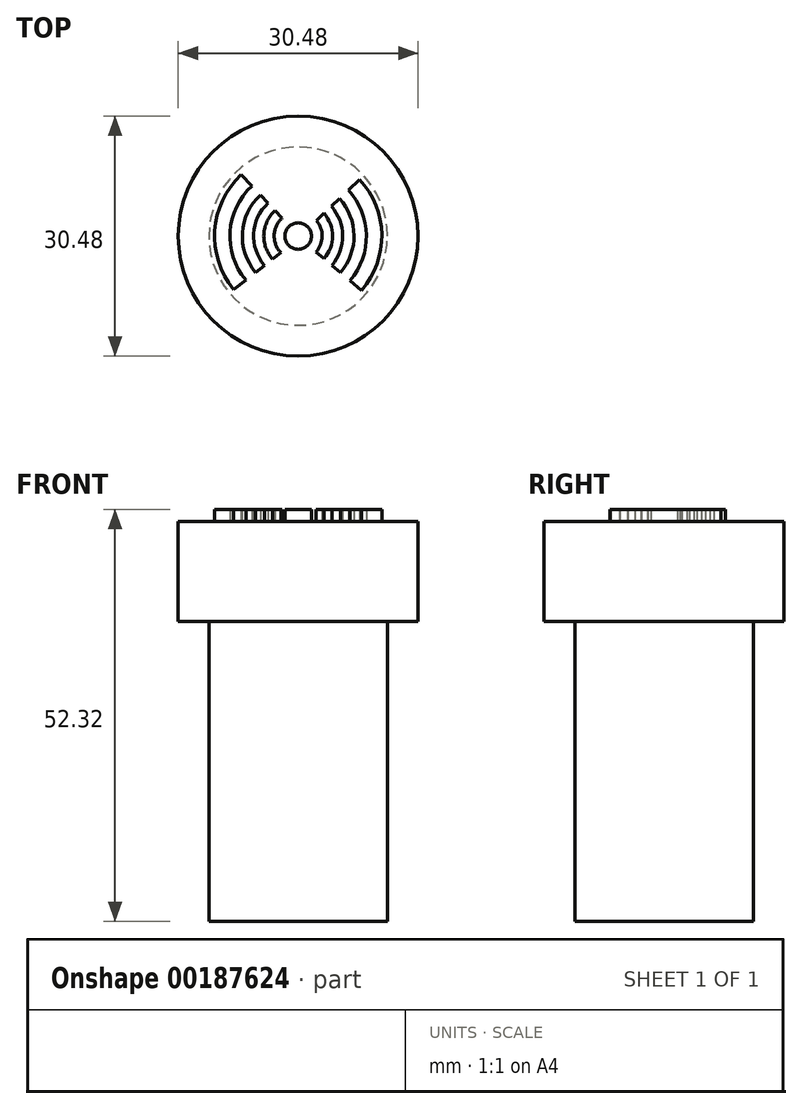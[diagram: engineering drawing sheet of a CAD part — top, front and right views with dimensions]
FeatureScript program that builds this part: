
annotation { "Feature Type Name" : "Feature", "Feature Type Description" : "" }
export const myFeature = defineFeature(function(context is Context, id is Id, definition is map)
    precondition{}
    {
        {
            var Q0;
            Q0=qCreatedBy(makeId("Top.planeOp"),FACE);
            var sketch = newSketch(context, id + "F0", { "sketchPlane" : qUnion([Q0])});
            skCircle(sketch, "E0", {"center": v(0, 0) * mm, "radius": 15.24 * mm});
            skCircle(sketch, "E1", {"center": v(0, 0) * mm, "radius": 11.33 * mm});
            skSolve(sketch);
        }
        {
            var Q0;
            Q0=makeQuery(id+"F0.imprint","IMPRINT",FACE,{"disambiguationData":[TD([[makeQuery(id+"F0.imprint","IMPRINT",EDGE,{"derivedFrom":sQuery(id+"F0.wireOp",EDGE,"E1")}),1.0]])]});
            extrude(context, id + "F1", {"entities" : qUnion([Q0]), "oppositeDirection" : true, "depth" : 50.8 * mm});
        }
        {
            var Q0;
            Q0 = qSketchRegion(id + "F0", true);
            extrude(context, id + "F2", {"entities" : qUnion([Q0]), "operationType" : NewBodyOperationType.ADD, "oppositeDirection" : true, "depth" : 12.7 * mm});
        }
        {
            var Q0;
            Q0=qCreatedBy(makeId("Top.planeOp"),FACE);
            var sketch = newSketch(context, id + "F3", { "sketchPlane" : qUnion([Q0])});
            skCircle(sketch, "E2", {"center": v(0, 0) * mm, "radius": 1.69 * mm});
            skArc(sketch, "E3", {"start": v(-2.02, 2.28) * mm, "mid": v(-3.04, 0.12) * mm, "end": v(-2.2, -2.12) * mm});
            skArc(sketch, "E4", {"start": v(-2.93, 3.24) * mm, "mid": v(-4.36, 0.22) * mm, "end": v(-3.24, -2.93) * mm});
            skArc(sketch, "E5", {"start": v(-3.82, 4.18) * mm, "mid": v(-5.65, 0.32) * mm, "end": v(-4.27, -3.72) * mm});
            skArc(sketch, "E6", {"start": v(-4.8, 5.22) * mm, "mid": v(-7.08, 0.43) * mm, "end": v(-5.4, -4.6) * mm});
            skArc(sketch, "E7", {"start": v(-5.89, 6.37) * mm, "mid": v(-8.66, 0.55) * mm, "end": v(-6.65, -5.57) * mm});
            skArc(sketch, "E8", {"start": v(-7.23, 7.78) * mm, "mid": v(-10.6, 0.7) * mm, "end": v(-8.2, -6.77) * mm});
            skLineSegment(sketch, "E9", {"start": v(-2.02, 2.28) * mm, "end": v(-2.93, 3.24) * mm});
            skLineSegment(sketch, "E10", {"start": v(2.3, 2) * mm, "end": v(3.26, 2.9) * mm});
            skLineSegment(sketch, "E11", {"start": v(-2.2, -2.12) * mm, "end": v(-3.24, -2.93) * mm});
            skLineSegment(sketch, "E12", {"start": v(2.27, -2.04) * mm, "end": v(3.28, -2.88) * mm});
            skArc(sketch, "E13.trimOffspring", {"start": v(3.28, -2.88) * mm, "mid": v(4.37, 0.01) * mm, "end": v(3.26, 2.9) * mm});
            skArc(sketch, "E14.trimOffspring", {"start": v(2.27, -2.04) * mm, "mid": v(3.05, -0.03) * mm, "end": v(2.3, 2) * mm});
            skArc(sketch, "E15.trimOffspring", {"start": v(4.28, -3.71) * mm, "mid": v(5.66, 0.05) * mm, "end": v(4.2, 3.79) * mm});
            skArc(sketch, "E16.trimOffspring", {"start": v(5.38, -4.63) * mm, "mid": v(7.1, 0.1) * mm, "end": v(5.25, 4.77) * mm});
            skArc(sketch, "E17.trimOffspring", {"start": v(6.59, -5.64) * mm, "mid": v(8.67, 0.14) * mm, "end": v(6.4, 5.85) * mm});
            skArc(sketch, "E18.trimOffspring", {"start": v(8.08, -6.9) * mm, "mid": v(10.62, 0.2) * mm, "end": v(7.82, 7.2) * mm});
            skLineSegment(sketch, "E19.trimOffspring", {"start": v(-3.82, 4.18) * mm, "end": v(-4.8, 5.22) * mm});
            skLineSegment(sketch, "E20.trimOffspring", {"start": v(-4.27, -3.72) * mm, "end": v(-5.4, -4.6) * mm});
            skLineSegment(sketch, "E21.trimOffspring", {"start": v(-6.65, -5.57) * mm, "end": v(-8.2, -6.77) * mm});
            skLineSegment(sketch, "E22.trimOffspring", {"start": v(-5.89, 6.37) * mm, "end": v(-7.23, 7.78) * mm});
            skLineSegment(sketch, "E23.trimOffspring", {"start": v(4.2, 3.79) * mm, "end": v(5.25, 4.77) * mm});
            skLineSegment(sketch, "E24.trimOffspring", {"start": v(4.28, -3.71) * mm, "end": v(5.38, -4.63) * mm});
            skLineSegment(sketch, "E25.trimOffspring", {"start": v(6.4, 5.85) * mm, "end": v(7.82, 7.2) * mm});
            skLineSegment(sketch, "E26.trimOffspring", {"start": v(6.59, -5.64) * mm, "end": v(8.08, -6.9) * mm});
            skSolve(sketch);
        }
        {
            var Q0;
            Q0 = qSketchRegion(id + "F3", true);
            extrude(context, id + "F4", {"entities" : qUnion([Q0]), "operationType" : NewBodyOperationType.ADD, "depth" : 1.52 * mm});
        }
    });
